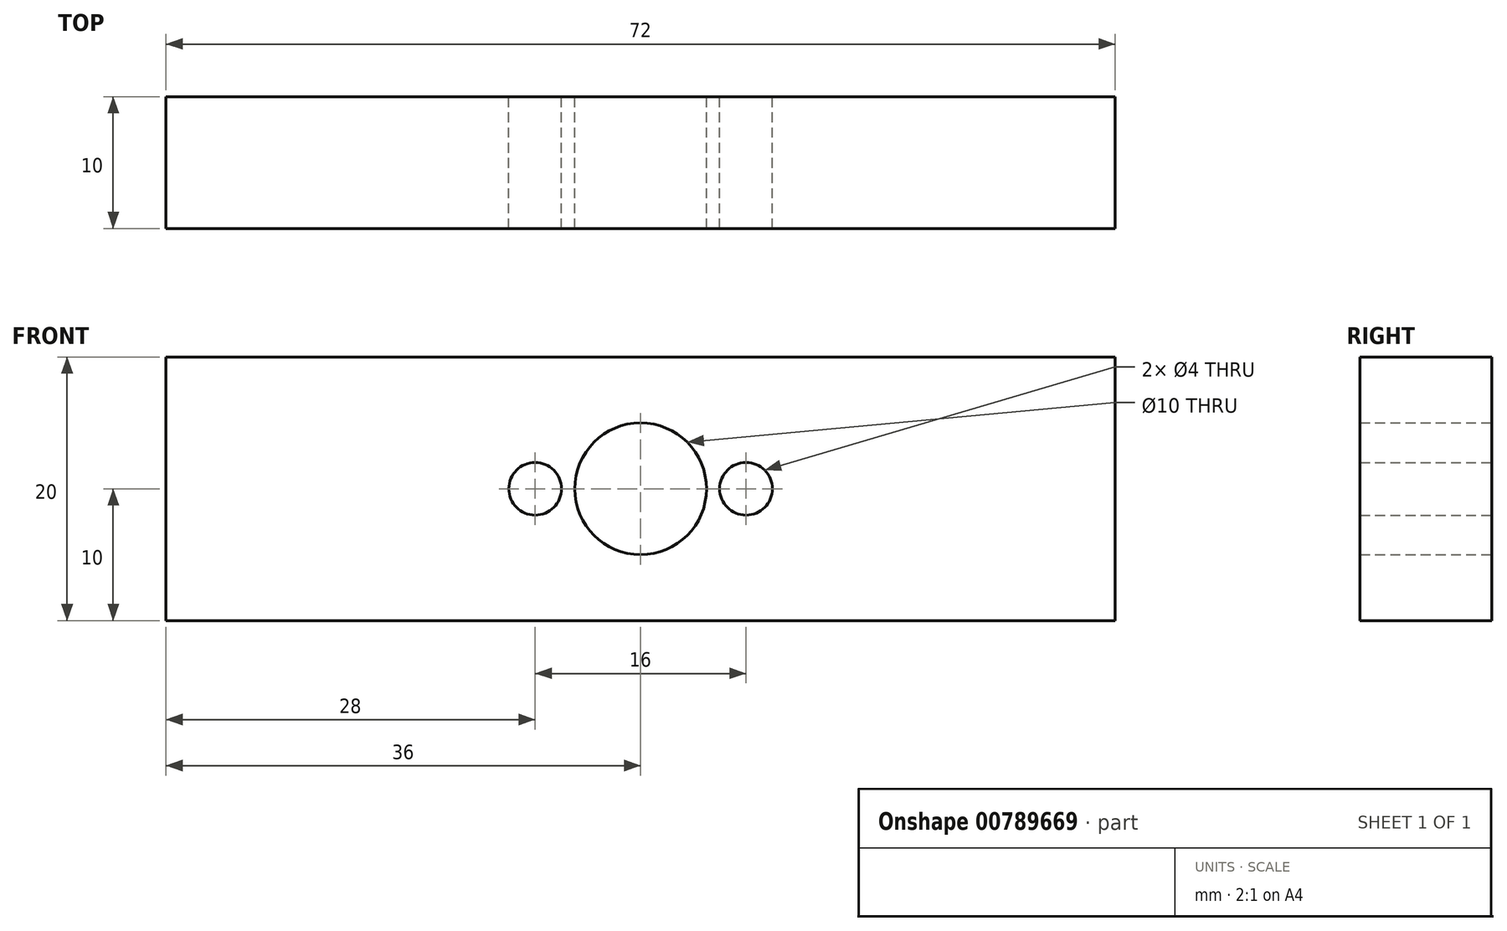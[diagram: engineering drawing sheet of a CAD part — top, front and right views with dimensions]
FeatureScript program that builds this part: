
annotation { "Feature Type Name" : "Feature", "Feature Type Description" : "" }
export const myFeature = defineFeature(function(context is Context, id is Id, definition is map)
    precondition{}
    {
        {
            var Q0;
            Q0=qCreatedBy(makeId("Front.planeOp"),FACE);
            var sketch = newSketch(context, id + "F0", { "sketchPlane" : qUnion([Q0])});
            skLineSegment(sketch, "E0.bottom", {"start": v(-72, 0) * mm, "end": v(0, 0) * mm});
            skLineSegment(sketch, "E0.top", {"start": v(-72, -20) * mm, "end": v(0, -20) * mm});
            skLineSegment(sketch, "E0.left", {"start": v(-72, 0) * mm, "end": v(-72, -20) * mm});
            skLineSegment(sketch, "E0.right", {"start": v(0, 0) * mm, "end": v(0, -20) * mm});
            skCircle(sketch, "E1", {"center": v(-36, -10) * mm, "radius": 5 * mm});
            skPoint(sketch, "E1.centerSnap0", {"position": v(-72, -10) * mm});
            skPoint(sketch, "E1.centerSnap1", {"position": v(-36, -20) * mm});
            skCircle(sketch, "E2", {"center": v(-44, -10) * mm, "radius": 2 * mm});
            skCircle(sketch, "E3", {"center": v(-28, -10) * mm, "radius": 2 * mm});
            skSolve(sketch);
        }
        {
            var Q0;
            Q0=qSketchRegion(id+"F0",true);
            var Q1;
            Q1=makeQuery(id+"F0.imprint","IMPRINT",FACE,{"disambiguationData":[TD([[makeQuery(id+"F0.imprint","IMPRINT",EDGE,{"derivedFrom":sQuery(id+"F0.wireOp",EDGE,"E0.bottom")}),-1.0]])]});
            extrude(context, id + "F1", {"entities" : qUnion([Q0, Q1]), "depth" : 10 * mm, "offsetDistance" : 25 * mm});
        }
    });
